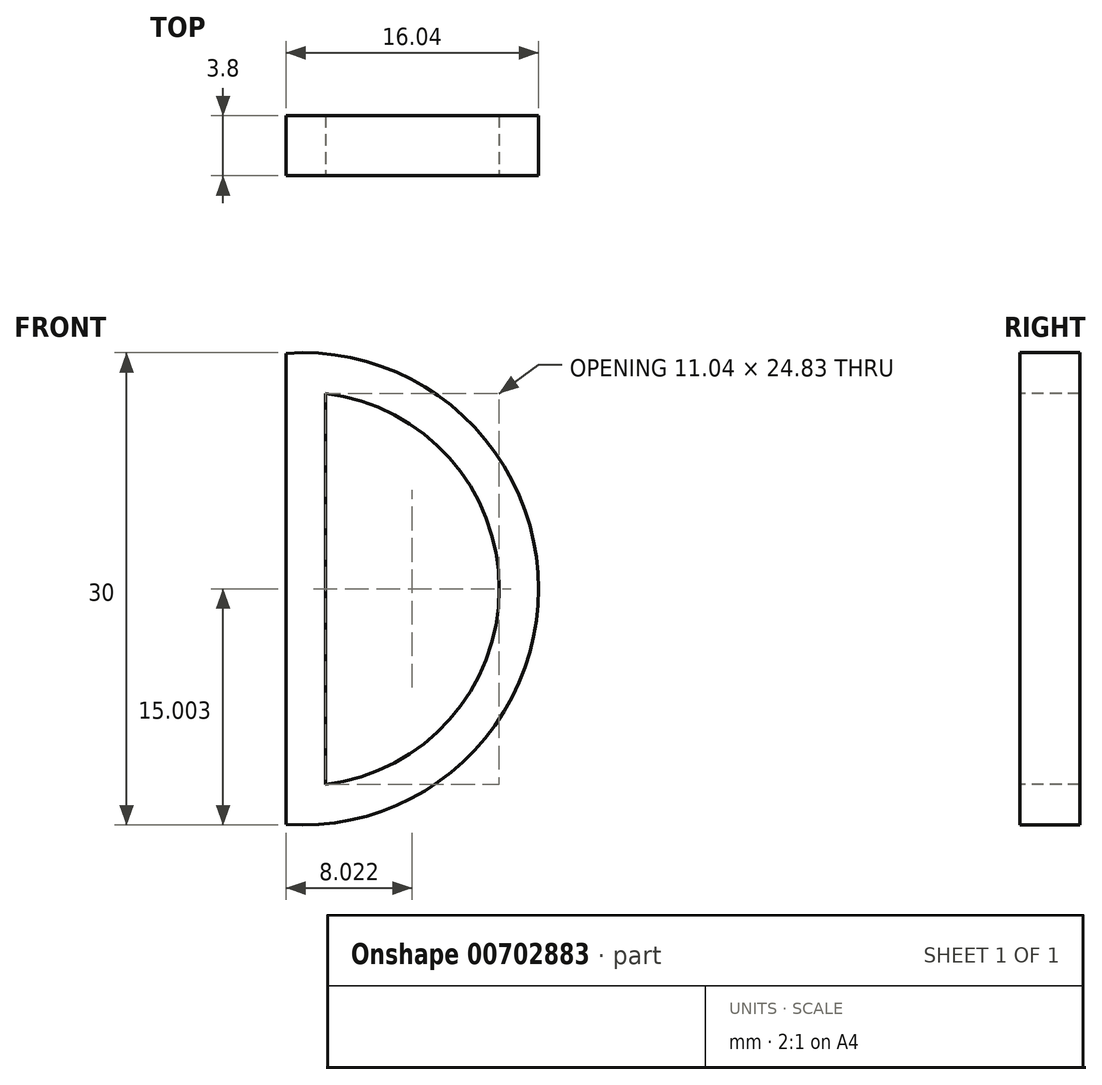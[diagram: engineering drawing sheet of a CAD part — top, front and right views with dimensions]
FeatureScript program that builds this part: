
annotation { "Feature Type Name" : "Feature", "Feature Type Description" : "" }
export const myFeature = defineFeature(function(context is Context, id is Id, definition is map)
    precondition{}
    {
        {
            var Q0;
            Q0=qCreatedBy(makeId("Front.planeOp"),FACE);
            var sketch = newSketch(context, id + "F0", { "sketchPlane" : qUnion([Q0])});
            skLineSegment(sketch, "E0", {"start": v(0, 15.73) * mm, "end": v(0, -14.2) * mm});
            skArc(sketch, "E1", {"start": v(0, -14.2) * mm, "mid": v(16.04, 0.76) * mm, "end": v(0, 15.73) * mm});
            skArc(sketch, "E2", {"start": v(2.09, -14.2) * mm, "mid": v(8.5, 1.28) * mm, "end": v(0, 15.73) * mm});
            skSolve(sketch);
        }
        {
            var Q0;
            Q0 = qSketchRegion(id + "F0", true);
            extrude(context, id + "F1", {"entities" : qUnion([Q0]), "oppositeDirection" : true, "depth" : 3.8 * mm, "offsetDistance" : 25.4 * mm});
        }
        {
            var Q0;
            Q0=makeQuery(id+"F1.opExtrude","CAP_FACE",FACE,{"disambiguationData":[OSD([sQuery(id+"F0.wireOp",EDGE,"E0"),sQuery(id+"F0.wireOp",EDGE,"E1")])],"isStart":true});
            var Q1;
            Q1=makeQuery(id+"F1.opExtrude","CAP_FACE",FACE,{"disambiguationData":[OSD([sQuery(id+"F0.wireOp",EDGE,"E0"),sQuery(id+"F0.wireOp",EDGE,"E1")])],"isStart":false});
            shell(context, id + "F2", {"entities" : qUnion([Q0, Q1]), "thickness" : 2.5 * mm});
        }
    });
